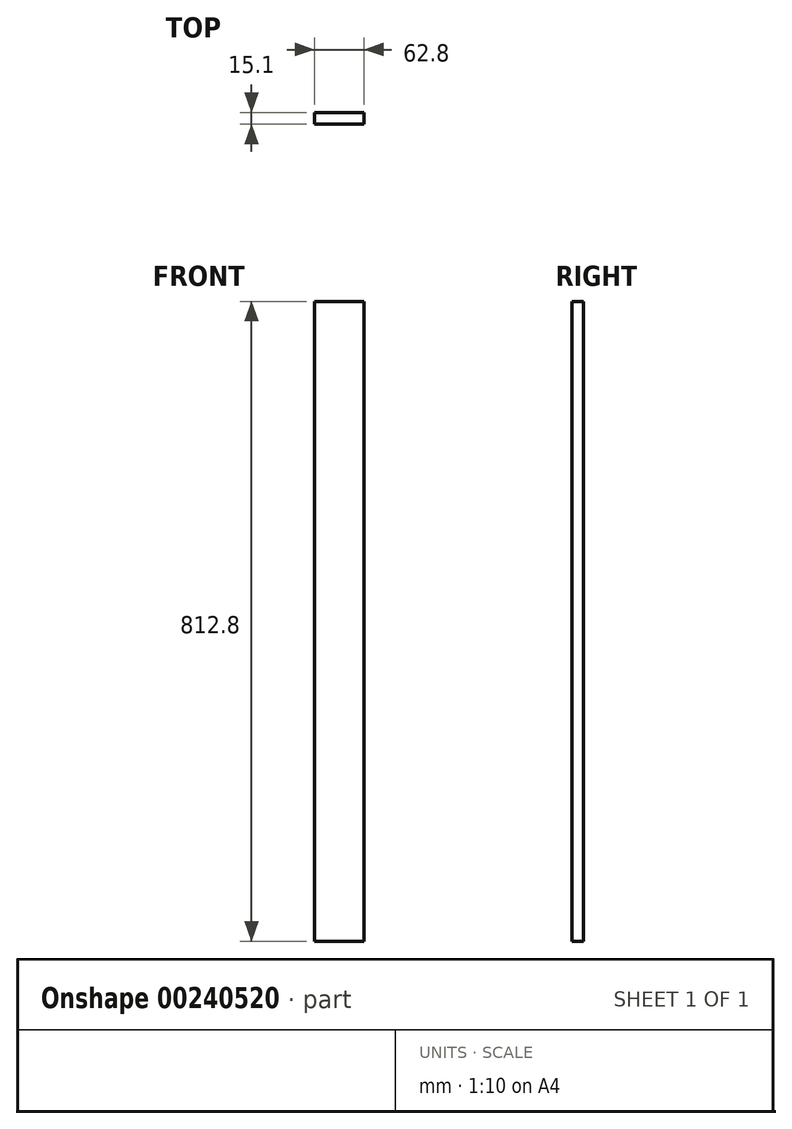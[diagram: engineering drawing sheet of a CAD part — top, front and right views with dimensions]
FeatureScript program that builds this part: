
annotation { "Feature Type Name" : "Feature", "Feature Type Description" : "" }
export const myFeature = defineFeature(function(context is Context, id is Id, definition is map)
    precondition{}
    {
        {
            var Q0;
            Q0=qCreatedBy(makeId("Top.planeOp"),FACE);
            var sketch = newSketch(context, id + "F0", { "sketchPlane" : qUnion([Q0])});
            skLineSegment(sketch, "E0.bottom", {"start": v(-34.4, 8.13) * mm, "end": v(28.4, 8.13) * mm});
            skLineSegment(sketch, "E0.top", {"start": v(-34.4, -6.97) * mm, "end": v(28.4, -6.97) * mm});
            skLineSegment(sketch, "E0.left", {"start": v(-34.4, 8.13) * mm, "end": v(-34.4, -6.97) * mm});
            skLineSegment(sketch, "E0.right", {"start": v(28.4, 8.13) * mm, "end": v(28.4, -6.97) * mm});
            skSolve(sketch);
        }
        {
            var Q0;
            Q0 = qSketchRegion(id + "F0", true);
            extrude(context, id + "F1", {"entities" : qUnion([Q0]), "depth" : 812.8 * mm});
        }
    });
